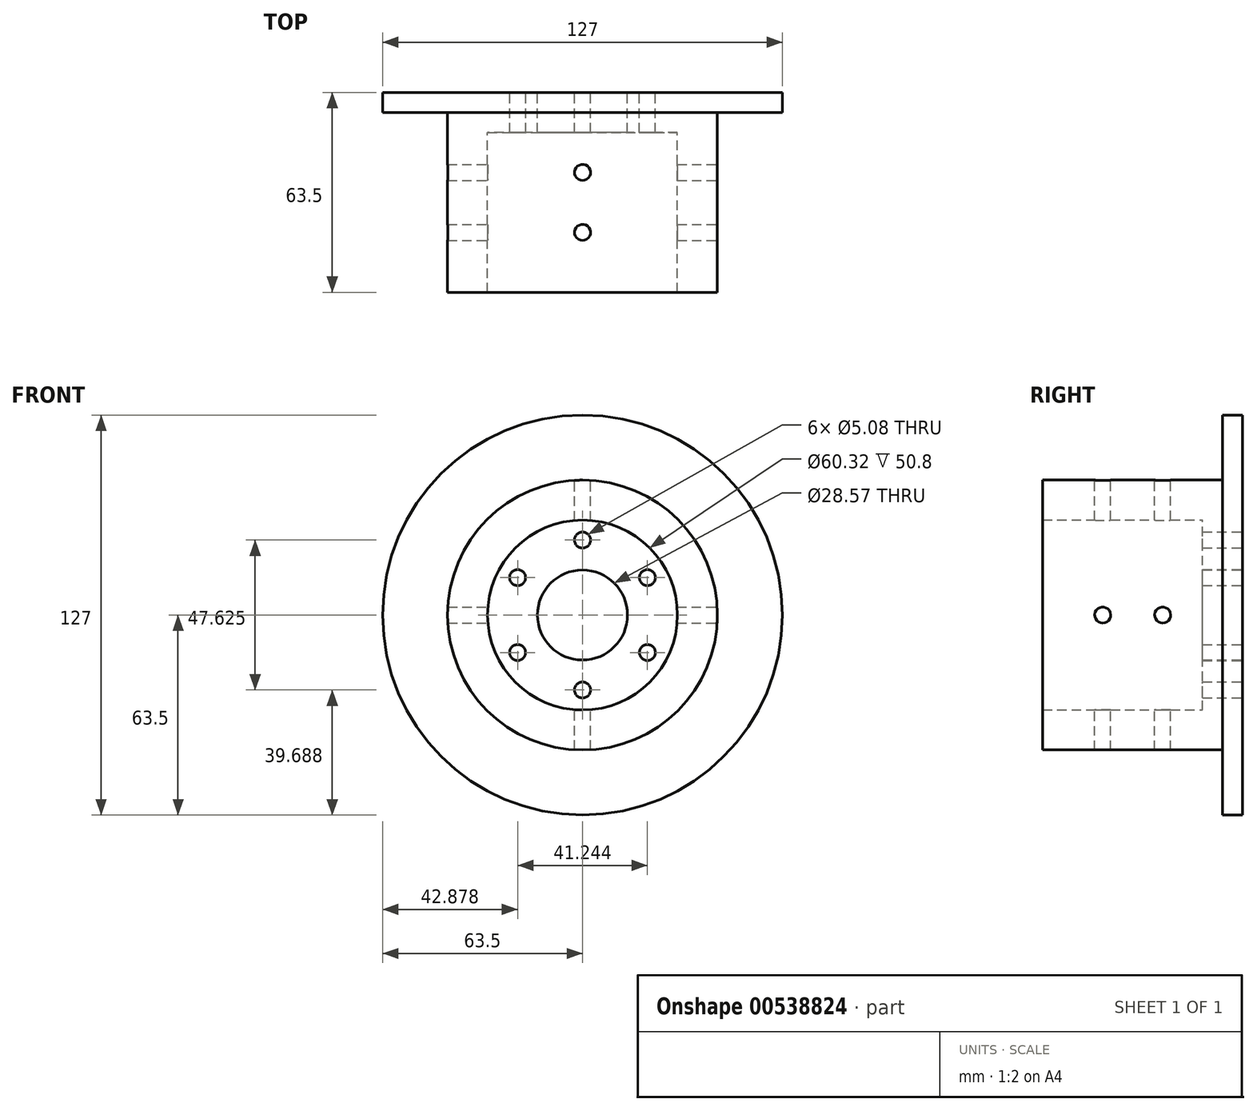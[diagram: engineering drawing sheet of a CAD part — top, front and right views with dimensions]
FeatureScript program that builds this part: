
annotation { "Feature Type Name" : "Feature", "Feature Type Description" : "" }
export const myFeature = defineFeature(function(context is Context, id is Id, definition is map)
    precondition{}
    {
        {
            var Q0;
            Q0=qCreatedBy(makeId("Front.planeOp"),FACE);
            var sketch = newSketch(context, id + "F0", { "sketchPlane" : qUnion([Q0])});
            skCircle(sketch, "E0", {"center": v(0, 0) * mm, "radius": 30.16 * mm});
            skCircle(sketch, "E1", {"center": v(0, 0) * mm, "radius": 42.86 * mm});
            skCircle(sketch, "E2", {"center": v(0, 0) * mm, "radius": 63.5 * mm});
            skCircle(sketch, "E3", {"center": v(0, 0) * mm, "radius": 23.81 * mm, "construction": true});
            skCircle(sketch, "E4", {"center": v(0, 23.81) * mm, "radius": 2.54 * mm});
            skCircle(sketch, "E5.1.0", {"center": v(-20.62, 11.9) * mm, "radius": 2.54 * mm});
            skCircle(sketch, "E5.2.0", {"center": v(-20.62, -11.9) * mm, "radius": 2.54 * mm});
            skCircle(sketch, "E5.3.0", {"center": v(0, -23.81) * mm, "radius": 2.54 * mm});
            skCircle(sketch, "E5.4.0", {"center": v(20.62, -11.9) * mm, "radius": 2.54 * mm});
            skCircle(sketch, "E5.5.0", {"center": v(20.62, 11.9) * mm, "radius": 2.54 * mm});
            skCircle(sketch, "E6", {"center": v(0, 0) * mm, "radius": 14.29 * mm});
            skCircle(sketch, "E7", {"center": v(0, 0) * mm, "radius": 26.25 * mm, "construction": true});
            skSolve(sketch);
        }
        {
            var Q0;
            Q0=makeQuery(id+"F0.imprint","IMPRINT",FACE,{"disambiguationData":[TD([[makeQuery(id+"F0.imprint","IMPRINT",EDGE,{"derivedFrom":sQuery(id+"F0.wireOp",EDGE,"E0")}),-1.0]])]});
            extrude(context, id + "F1", {"entities" : qUnion([Q0]), "depth" : 63.5 * mm, "offsetDistance" : 25.4 * mm});
        }
        {
            var Q0;
            Q0=makeQuery(id+"F0.imprint","IMPRINT",FACE,{"disambiguationData":[TD([[makeQuery(id+"F0.imprint","IMPRINT",EDGE,{"derivedFrom":sQuery(id+"F0.wireOp",EDGE,"E1")}),-1.0]])]});
            extrude(context, id + "F2", {"entities" : qUnion([Q0]), "operationType" : NewBodyOperationType.ADD, "depth" : 6.35 * mm, "offsetDistance" : 25.4 * mm});
        }
        {
            var Q0;
            Q0=makeQuery(id+"F0.imprint","IMPRINT",FACE,{"disambiguationData":[TD([[makeQuery(id+"F0.imprint","IMPRINT",EDGE,{"derivedFrom":sQuery(id+"F0.wireOp",EDGE,"E0")}),1.0]])]});
            extrude(context, id + "F3", {"entities" : qUnion([Q0]), "operationType" : NewBodyOperationType.ADD, "depth" : 12.7 * mm, "offsetDistance" : 25.4 * mm});
        }
        {
            var Q0;
            Q0=qCreatedBy(makeId("Right.planeOp"),FACE);
            cPlane(context, id + "F4", {"entities" : qUnion([Q0]), "cplaneType" : CPlaneType.OFFSET, "offset" : 45.2 * mm, "width" : 152.4 * mm, "height" : 152.4 * mm});
        }
        {
            var Q0;
            Q0=qCreatedBy(id+"F4.planeOp",FACE);
            var sketch = newSketch(context, id + "F5", { "sketchPlane" : qUnion([Q0])});
            skCircle(sketch, "E8", {"center": v(-25.4, 0) * mm, "radius": 2.54 * mm});
            skCircle(sketch, "E9", {"center": v(-44.45, 0) * mm, "radius": 2.54 * mm});
            skSolve(sketch);
        }
        {
            var Q0;
            Q0 = qSketchRegion(id + "F5", true);
            var Q1;
            Q1=makeQuery(id+"F1.opExtrude","SWEPT_FACE",FACE,{"disambiguationData":[OSD([sQuery(id+"F0.wireOp",EDGE,"E1")])]});
            extrude(context, id + "F6", {"entities" : qUnion([Q0]), "operationType" : NewBodyOperationType.REMOVE, "oppositeDirection" : true, "depth" : 101.6 * mm, "endBoundEntityFace" : qUnion([Q1]), "offsetDistance" : 25.4 * mm});
        }
        {
            var Q0;
            Q0=qCreatedBy(makeId("Top.planeOp"),FACE);
            cPlane(context, id + "F7", {"entities" : qUnion([Q0]), "cplaneType" : CPlaneType.OFFSET, "offset" : 44.2 * mm, "width" : 152.4 * mm, "height" : 152.4 * mm});
        }
        {
            var Q0;
            Q0=qCreatedBy(id+"F7.planeOp",FACE);
            var sketch = newSketch(context, id + "F8", { "sketchPlane" : qUnion([Q0])});
            skCircle(sketch, "E10", {"center": v(0, -25.4) * mm, "radius": 2.54 * mm});
            skCircle(sketch, "E11", {"center": v(0, -44.45) * mm, "radius": 2.54 * mm});
            skSolve(sketch);
        }
        {
            var Q0;
            Q0 = qSketchRegion(id + "F8", true);
            extrude(context, id + "F9", {"entities" : qUnion([Q0]), "operationType" : NewBodyOperationType.REMOVE, "oppositeDirection" : true, "depth" : 101.6 * mm, "offsetDistance" : 25.4 * mm});
        }
    });
